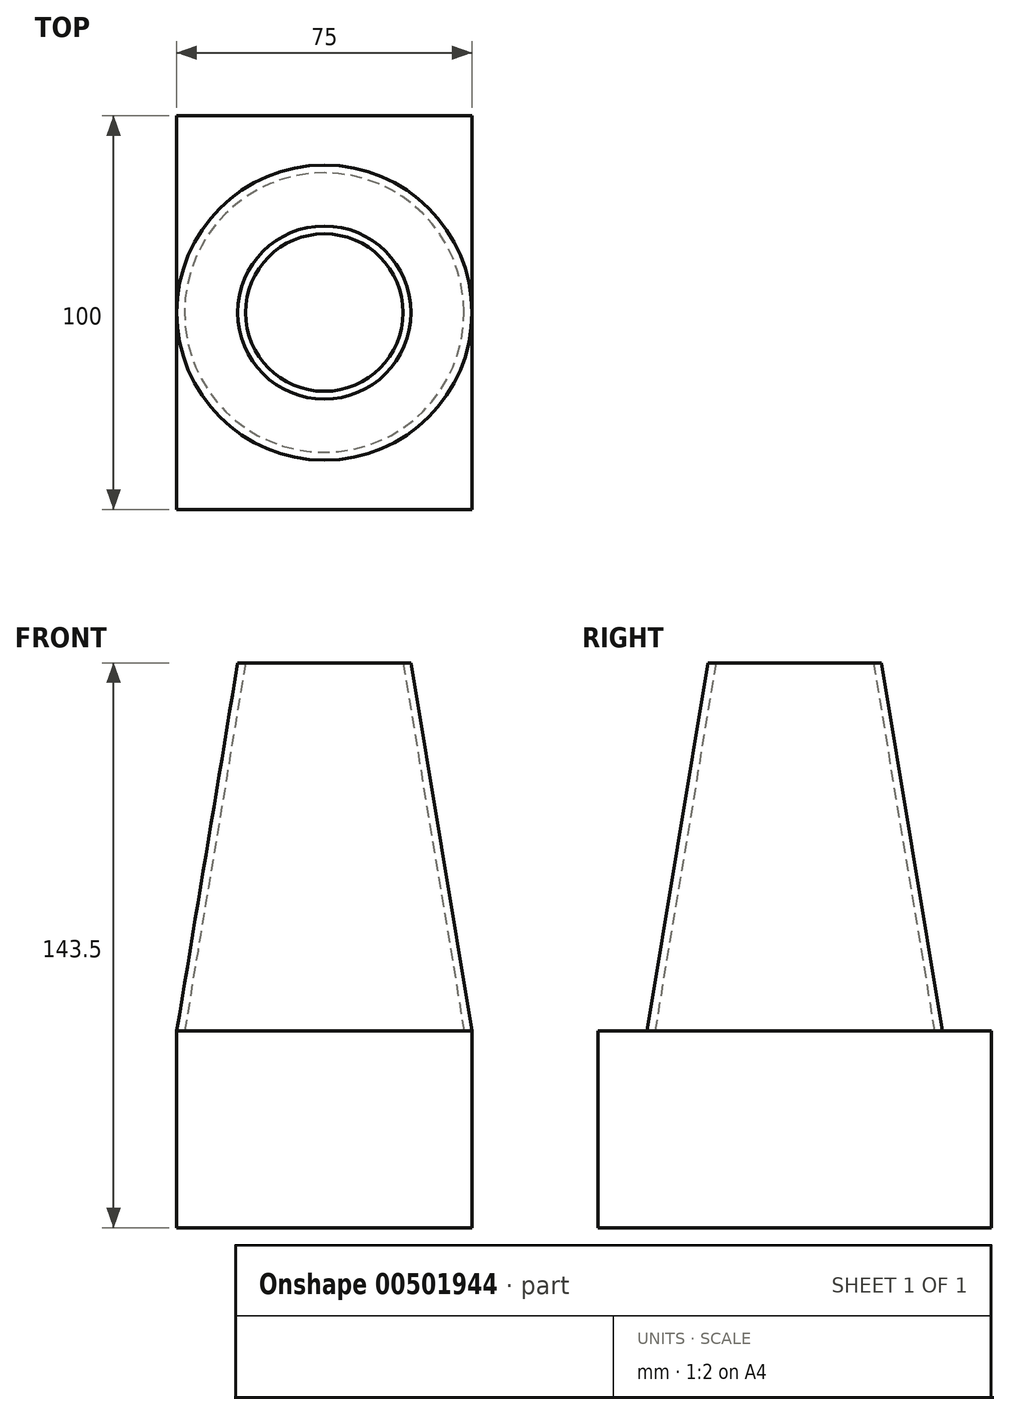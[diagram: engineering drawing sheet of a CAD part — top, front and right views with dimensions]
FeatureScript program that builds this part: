
annotation { "Feature Type Name" : "Feature", "Feature Type Description" : "" }
export const myFeature = defineFeature(function(context is Context, id is Id, definition is map)
    precondition{}
    {
        {
            var Q0;
            Q0=qCreatedBy(makeId("Top.planeOp"),FACE);
            var sketch = newSketch(context, id + "F0", { "sketchPlane" : qUnion([Q0])});
            skLineSegment(sketch, "E0.bottom", {"start": v(37.5, -50) * mm, "end": v(-37.5, -50) * mm});
            skLineSegment(sketch, "E0.top", {"start": v(37.5, 50) * mm, "end": v(-37.5, 50) * mm});
            skLineSegment(sketch, "E0.left", {"start": v(37.5, -50) * mm, "end": v(37.5, 50) * mm});
            skLineSegment(sketch, "E0.right", {"start": v(-37.5, -50) * mm, "end": v(-37.5, 50) * mm});
            skPoint(sketch, "E0.middle", {"position": v(0, 0) * mm});
            skSolve(sketch);
        }
        {
            var Q0;
            Q0=makeQuery(id+"F0.imprint","IMPRINT",FACE,{"disambiguationData":[TD([[makeQuery(id+"F0.imprint","IMPRINT",EDGE,{"derivedFrom":sQuery(id+"F0.wireOp",EDGE,"E0.bottom")}),-1.0]])]});
            extrude(context, id + "F1", {"entities" : qUnion([Q0]), "oppositeDirection" : true, "depth" : 50 * mm});
        }
        {
            var Q0;
            Q0=qCreatedBy(makeId("Right.planeOp"),FACE);
            var sketch = newSketch(context, id + "F2", { "sketchPlane" : qUnion([Q0])});
            skLineSegment(sketch, "E1", {"start": v(-20, 93.5) * mm, "end": v(-35.5, 0) * mm});
            skLineSegment(sketch, "E2", {"start": v(-35.5, 0) * mm, "end": v(-37.5, 0) * mm});
            skLineSegment(sketch, "E3", {"start": v(-37.5, 0) * mm, "end": v(-22, 93.5) * mm});
            skLineSegment(sketch, "E4", {"start": v(-22, 93.5) * mm, "end": v(-20, 93.5) * mm});
            skLineSegment(sketch, "E5", {"start": v(0, 0) * mm, "end": v(0, 93.5) * mm, "construction": true});
            skSolve(sketch);
        }
        {
            var Q0;
            Q0=makeQuery(id+"F2.imprint","IMPRINT",FACE,{"disambiguationData":[TD([[makeQuery(id+"F2.imprint","IMPRINT",EDGE,{"derivedFrom":sQuery(id+"F2.wireOp",EDGE,"E1")}),-1.0]])]});
            var Q1;
            Q1=sQuery(id+"F2.wireOp",EDGE,"E5");
            revolve(context, id + "F3", {"operationType" : NewBodyOperationType.ADD, "entities" : qUnion([Q0]), "axis" : qUnion([Q1]), "revolveType" : RevolveType.FULL});
        }
    });
